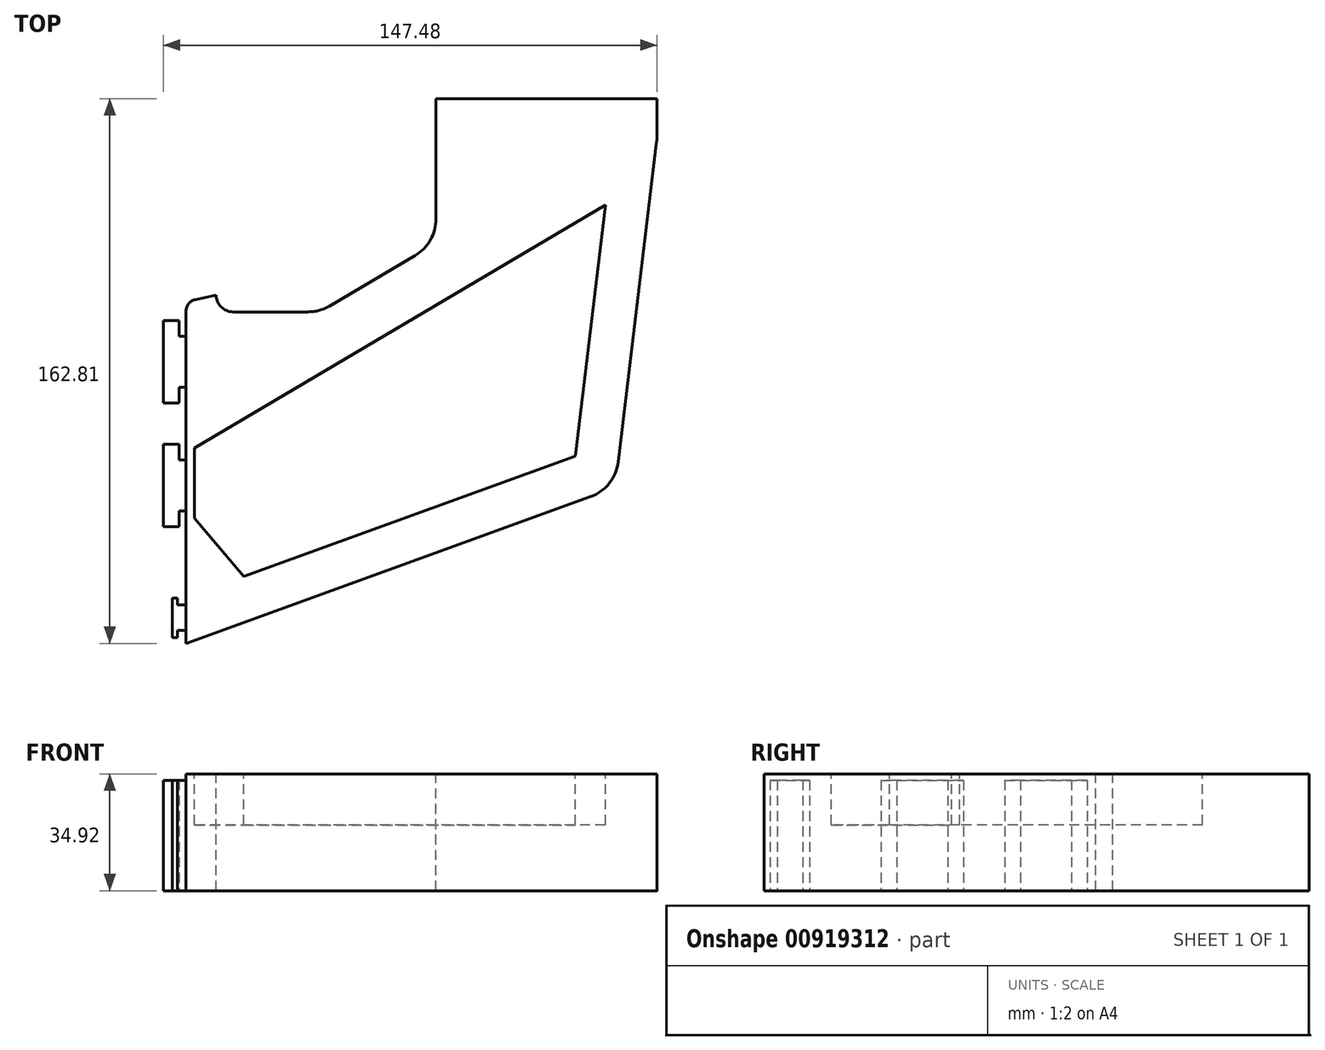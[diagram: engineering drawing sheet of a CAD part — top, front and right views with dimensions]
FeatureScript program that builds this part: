
annotation { "Feature Type Name" : "Feature", "Feature Type Description" : "" }
export const myFeature = defineFeature(function(context is Context, id is Id, definition is map)
    precondition{}
    {
        {
            var Q0;
            Q0=qCreatedBy(makeId("Top.planeOp"),FACE);
            var sketch = newSketch(context, id + "F0", { "sketchPlane" : qUnion([Q0])});
            skLineSegment(sketch, "E0", {"start": v(0, 51.05) * mm, "end": v(0, -51.05) * mm});
            skLineSegment(sketch, "E1", {"start": v(0, -51.05) * mm, "end": v(128.22, -4.53) * mm});
            skLineSegment(sketch, "E2", {"start": v(140.72, 99.82) * mm, "end": v(140.72, 111.76) * mm});
            skLineSegment(sketch, "E3", {"start": v(140.72, 111.76) * mm, "end": v(74.68, 111.76) * mm});
            skLineSegment(sketch, "E4", {"start": v(74.68, 111.76) * mm, "end": v(74.68, 68.58) * mm});
            skLineSegment(sketch, "E5", {"start": v(74.68, 68.58) * mm, "end": v(39.88, 48) * mm});
            skLineSegment(sketch, "E6", {"start": v(39.88, 48) * mm, "end": v(9.02, 48) * mm});
            skLineSegment(sketch, "E7", {"start": v(0, 51.05) * mm, "end": v(9.02, 53.09) * mm});
            skLineSegment(sketch, "E8", {"start": v(9.02, 53.09) * mm, "end": v(9.02, 48) * mm});
            skLineSegment(sketch, "E9", {"start": v(140.72, 99.82) * mm, "end": v(128.22, -4.53) * mm});
            skPoint(sketch, "E10.orphan", {"position": v(140.72, 0) * mm});
            skSolve(sketch);
        }
        {
            var Q0;
            Q0 = qSketchRegion(id + "F0", true);
            extrude(context, id + "F1", {"entities" : qUnion([Q0]), "oppositeDirection" : true, "depth" : 34.92 * mm, "offsetDistance" : 25.4 * mm});
        }
        {
            var Q0;
            Q0=makeQuery(id+"F1.opExtrude","CAP_FACE",FACE,{"disambiguationData":[OSD([sQuery(id+"F0.wireOp",EDGE,"E0"),sQuery(id+"F0.wireOp",EDGE,"E1"),sQuery(id+"F0.wireOp",EDGE,"E2"),sQuery(id+"F0.wireOp",EDGE,"E3"),sQuery(id+"F0.wireOp",EDGE,"E4"),sQuery(id+"F0.wireOp",EDGE,"E5"),sQuery(id+"F0.wireOp",EDGE,"E6"),sQuery(id+"F0.wireOp",EDGE,"E7"),sQuery(id+"F0.wireOp",EDGE,"E8"),sQuery(id+"F0.wireOp",EDGE,"E9")])],"isStart":false});
            var sketch = newSketch(context, id + "F2", { "sketchPlane" : qUnion([Q0])});
            skLineSegment(sketch, "E11.0", {"start": v(0, -51.05) * mm, "end": v(0, 51.05) * mm});
            skLineSegment(sketch, "E12", {"start": v(0, 47.18) * mm, "end": v(-2.54, 47.18) * mm});
            skLineSegment(sketch, "E13", {"start": v(-2.54, 47.18) * mm, "end": v(-2.54, 49.28) * mm});
            skLineSegment(sketch, "E14", {"start": v(-2.54, 49.28) * mm, "end": v(-4.06, 49.28) * mm});
            skLineSegment(sketch, "E15", {"start": v(-4.06, 49.28) * mm, "end": v(-4.06, 37.46) * mm});
            skLineSegment(sketch, "E16", {"start": v(-4.06, 37.46) * mm, "end": v(-2.54, 37.46) * mm});
            skLineSegment(sketch, "E17", {"start": v(-2.54, 37.46) * mm, "end": v(-2.54, 39.56) * mm});
            skLineSegment(sketch, "E18", {"start": v(-2.54, 39.56) * mm, "end": v(0, 39.56) * mm});
            skLineSegment(sketch, "E19", {"start": v(0, 11.43) * mm, "end": v(-2.06, 11.43) * mm});
            skLineSegment(sketch, "E20", {"start": v(-2.06, 11.43) * mm, "end": v(-2.06, 16.13) * mm});
            skLineSegment(sketch, "E21", {"start": v(-2.06, 16.13) * mm, "end": v(-6.76, 16.13) * mm});
            skLineSegment(sketch, "E22", {"start": v(-6.76, 16.13) * mm, "end": v(-6.76, -8.5) * mm});
            skLineSegment(sketch, "E23", {"start": v(-6.76, -8.5) * mm, "end": v(-2.06, -8.5) * mm});
            skLineSegment(sketch, "E24", {"start": v(-2.06, -8.5) * mm, "end": v(-2.06, -3.81) * mm});
            skLineSegment(sketch, "E25", {"start": v(-2.06, -3.81) * mm, "end": v(0, -3.81) * mm});
            skLineSegment(sketch, "E26", {"start": v(0, -25.53) * mm, "end": v(-2.06, -25.53) * mm});
            skLineSegment(sketch, "E27", {"start": v(-2.06, -25.53) * mm, "end": v(-2.06, -20.83) * mm});
            skLineSegment(sketch, "E28", {"start": v(-2.06, -20.83) * mm, "end": v(-6.76, -20.83) * mm});
            skLineSegment(sketch, "E29", {"start": v(-6.76, -20.83) * mm, "end": v(-6.76, -45.47) * mm});
            skLineSegment(sketch, "E30", {"start": v(-6.76, -45.47) * mm, "end": v(-2.06, -45.47) * mm});
            skLineSegment(sketch, "E31", {"start": v(-2.06, -45.47) * mm, "end": v(-2.06, -40.77) * mm});
            skLineSegment(sketch, "E32", {"start": v(-2.06, -40.77) * mm, "end": v(0, -40.77) * mm});
            skSolve(sketch);
        }
        {
            var Q0;
            Q0 = qSketchRegion(id + "F2", true);
            extrude(context, id + "F3", {"entities" : qUnion([Q0]), "operationType" : NewBodyOperationType.ADD, "oppositeDirection" : true, "depth" : 33.02 * mm, "offsetDistance" : 25.4 * mm});
        }
        {
            var Q0;
            Q0=makeQuery(id+"F1.opExtrude","SWEPT_EDGE",EDGE,{"disambiguationData":[OSD([sQuery(id+"F0.wireOp",EDGE,"E5"),sQuery(id+"F0.wireOp",EDGE,"E6")])]});
            var Q1;
            Q1=makeQuery(id+"F1.opExtrude","SWEPT_EDGE",EDGE,{"disambiguationData":[OSD([sQuery(id+"F0.wireOp",EDGE,"E4"),sQuery(id+"F0.wireOp",EDGE,"E5")])]});
            var Q2;
            Q2=makeQuery(id+"F1.opExtrude","SWEPT_EDGE",EDGE,{"disambiguationData":[OSD([sQuery(id+"F0.wireOp",EDGE,"E1"),sQuery(id+"F0.wireOp",EDGE,"E9")])]});
            var Q3;
            Q3=makeQuery(id+"F1.opExtrude","SWEPT_EDGE",EDGE,{"disambiguationData":[OSD([sQuery(id+"F0.wireOp",EDGE,"E2"),sQuery(id+"F0.wireOp",EDGE,"E9")])]});
            fillet(context, id + "F4", {"entities" : qUnion([Q0, Q1, Q2, Q3]), "radius" : 12.7 * mm, "tangentPropagation" : true, "allowEdgeOverflow" : false});
        }
        {
            var Q0;
            Q0=makeQuery(id+"F1.opExtrude","SWEPT_EDGE",EDGE,{"disambiguationData":[OSD([sQuery(id+"F0.wireOp",EDGE,"E6"),sQuery(id+"F0.wireOp",EDGE,"E8")])]});
            fillet(context, id + "F5", {"entities" : qUnion([Q0]), "radius" : 5.08 * mm, "tangentPropagation" : true, "allowEdgeOverflow" : false});
        }
        {
            var Q0;
            Q0=makeQuery(id+"F1.opExtrude","SWEPT_EDGE",EDGE,{"disambiguationData":[OSD([sQuery(id+"F0.wireOp",EDGE,"E0"),sQuery(id+"F0.wireOp",EDGE,"E7")])]});
            fillet(context, id + "F6", {"entities" : qUnion([Q0]), "radius" : 3.56 * mm, "tangentPropagation" : true, "allowEdgeOverflow" : false});
        }
        {
            var Q0;
            Q0=makeQuery(id+"F1.opExtrude","CAP_FACE",FACE,{"disambiguationData":[OSD([sQuery(id+"F0.wireOp",EDGE,"E0"),sQuery(id+"F0.wireOp",EDGE,"E1"),sQuery(id+"F0.wireOp",EDGE,"E2"),sQuery(id+"F0.wireOp",EDGE,"E3"),sQuery(id+"F0.wireOp",EDGE,"E4"),sQuery(id+"F0.wireOp",EDGE,"E5"),sQuery(id+"F0.wireOp",EDGE,"E6"),sQuery(id+"F0.wireOp",EDGE,"E7"),sQuery(id+"F0.wireOp",EDGE,"E8"),sQuery(id+"F0.wireOp",EDGE,"E9")])],"isStart":true});
            var sketch = newSketch(context, id + "F7", { "sketchPlane" : qUnion([Q0])});
            skLineSegment(sketch, "E33.0", {"start": v(125.29, 79.91) * mm, "end": v(116.3, 4.92) * mm});
            skLineSegment(sketch, "E33.2", {"start": v(17.27, -31) * mm, "end": v(116.3, 4.92) * mm});
            skLineSegment(sketch, "E34.0", {"start": v(125.29, 79.91) * mm, "end": v(2.54, 7.34) * mm});
            skLineSegment(sketch, "E35", {"start": v(2.54, 7.34) * mm, "end": v(2.54, -13.59) * mm});
            skLineSegment(sketch, "E36", {"start": v(2.54, -13.59) * mm, "end": v(17.27, -31) * mm});
            skSolve(sketch);
        }
        {
            var Q0;
            Q0 = qSketchRegion(id + "F7", true);
            extrude(context, id + "F8", {"entities" : qUnion([Q0]), "operationType" : NewBodyOperationType.REMOVE, "oppositeDirection" : true, "depth" : 15.24 * mm, "offsetDistance" : 25.4 * mm});
        }
    });
